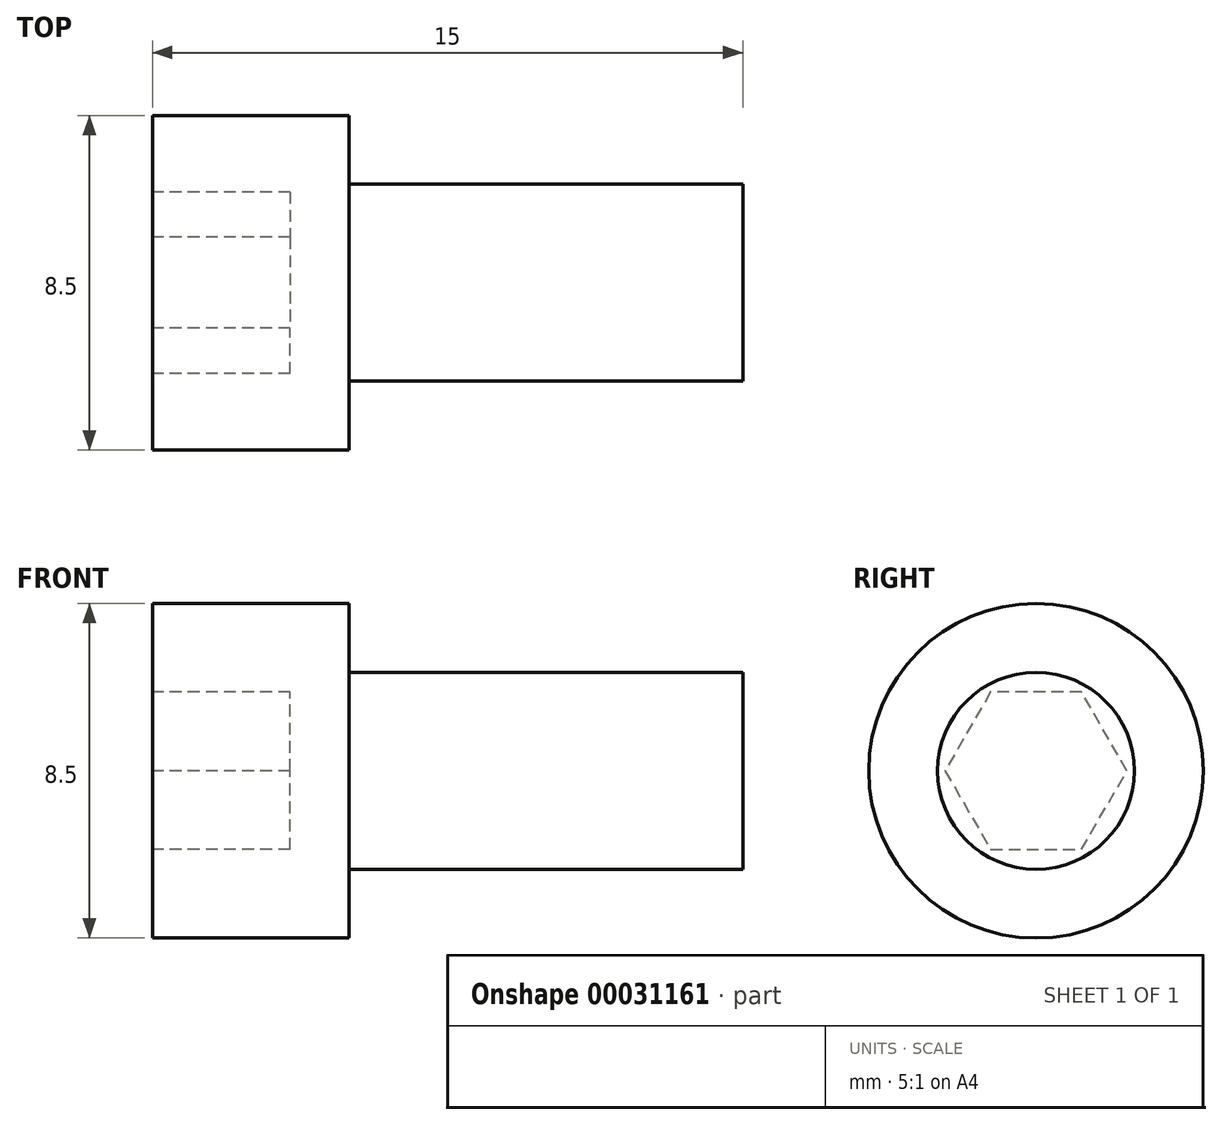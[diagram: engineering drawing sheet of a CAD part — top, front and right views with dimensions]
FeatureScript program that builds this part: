
annotation { "Feature Type Name" : "Feature", "Feature Type Description" : "" }
export const myFeature = defineFeature(function(context is Context, id is Id, definition is map)
    precondition{}
    {
        {
            var Q0;
            Q0=qCreatedBy(makeId("Front.planeOp"),FACE);
            var sketch = newSketch(context, id + "F0", { "sketchPlane" : qUnion([Q0])});
            skLineSegment(sketch, "E0", {"start": v(0, 0) * mm, "end": v(5, 0) * mm});
            skLineSegment(sketch, "E1", {"start": v(5, 0) * mm, "end": v(5, -1.75) * mm});
            skLineSegment(sketch, "E2", {"start": v(5, -1.75) * mm, "end": v(15, -1.75) * mm});
            skLineSegment(sketch, "E3", {"start": v(15, -1.75) * mm, "end": v(15, -4.25) * mm});
            skLineSegment(sketch, "E4", {"start": v(15, -4.25) * mm, "end": v(0, -4.25) * mm});
            skLineSegment(sketch, "E5", {"start": v(0, -4.25) * mm, "end": v(0, 0) * mm});
            skSolve(sketch);
        }
        {
            var Q0;
            Q0 = qSketchRegion(id + "F0", true);
            var Q1;
            Q1=sQuery(id+"F0.wireOp",EDGE,"E4");
            revolve(context, id + "F1", {"entities" : qUnion([Q0]), "axis" : qUnion([Q1]), "revolveType" : RevolveType.FULL});
        }
        {
            var Q0;
            Q0=makeQuery(id+"F1.opRevolve","SWEPT_FACE",FACE,{"disambiguationData":[OSD([sQuery(id+"F0.wireOp",EDGE,"E5")])]});
            var sketch = newSketch(context, id + "F2", { "sketchPlane" : qUnion([Q0])});
            skCircle(sketch, "E6.cCircle", {"center": v(0, -4.25) * mm, "radius": 2 * mm, "construction": true});
            skLineSegment(sketch, "E6.0", {"start": v(-1.15, -2.25) * mm, "end": v(1.15, -2.25) * mm});
            skLineSegment(sketch, "E6.1", {"start": v(1.15, -2.25) * mm, "end": v(2.3, -4.25) * mm});
            skLineSegment(sketch, "E6.2", {"start": v(2.3, -4.25) * mm, "end": v(1.15, -6.25) * mm});
            skLineSegment(sketch, "E6.3", {"start": v(1.15, -6.25) * mm, "end": v(-1.15, -6.25) * mm});
            skLineSegment(sketch, "E6.4", {"start": v(-1.15, -6.25) * mm, "end": v(-2.3, -4.25) * mm});
            skLineSegment(sketch, "E6.5", {"start": v(-2.3, -4.25) * mm, "end": v(-1.15, -2.25) * mm});
            skPoint(sketch, "E6.0.midPoint", {"position": v(0, -2.25) * mm});
            skSolve(sketch);
        }
        {
            var Q0;
            Q0 = qSketchRegion(id + "F2", true);
            extrude(context, id + "F3", {"entities" : qUnion([Q0]), "operationType" : NewBodyOperationType.REMOVE, "oppositeDirection" : true, "depth" : 3.5 * mm});
        }
    });
